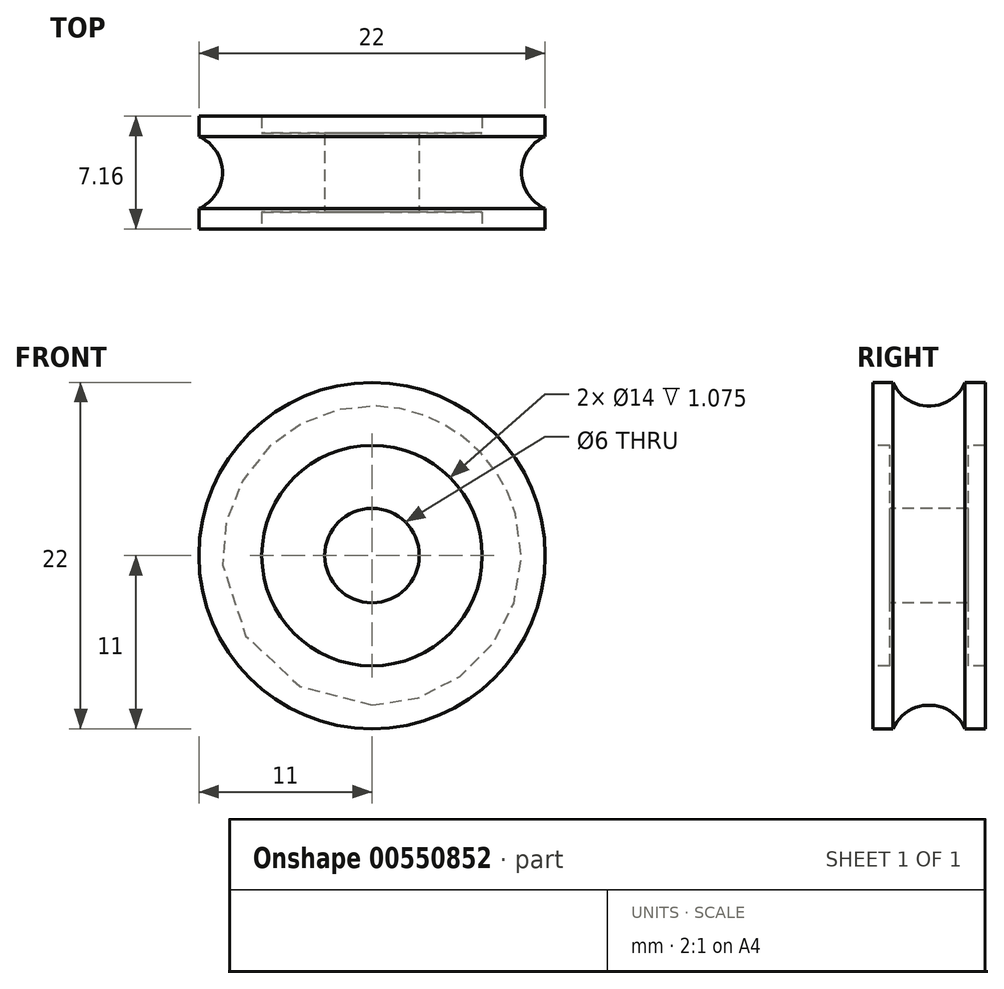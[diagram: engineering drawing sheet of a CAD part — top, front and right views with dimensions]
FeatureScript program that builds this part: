
annotation { "Feature Type Name" : "Feature", "Feature Type Description" : "" }
export const myFeature = defineFeature(function(context is Context, id is Id, definition is map)
    precondition{}
    {
        {
            var Q0;
            Q0=qCreatedBy(makeId("Right.planeOp"),FACE);
            var sketch = newSketch(context, id + "F0", { "sketchPlane" : qUnion([Q0])});
            skLineSegment(sketch, "E0", {"start": v(0, 0) * mm, "end": v(9.5, 0) * mm, "construction": true});
            skLineSegment(sketch, "E1", {"start": v(0, 0) * mm, "end": v(0, 3) * mm, "construction": true});
            skLineSegment(sketch, "E2", {"start": v(-2.5, 3) * mm, "end": v(2.5, 3) * mm});
            skLineSegment(sketch, "E3", {"start": v(2.5, 3) * mm, "end": v(2.5, 7) * mm});
            skLineSegment(sketch, "E4", {"start": v(2.5, 7) * mm, "end": v(3.58, 7) * mm});
            skLineSegment(sketch, "E5", {"start": v(3.58, 7) * mm, "end": v(3.58, 11) * mm});
            skLineSegment(sketch, "E6", {"start": v(3.58, 11) * mm, "end": v(2.3, 11) * mm});
            skLineSegment(sketch, "E7.MirrorCS", {"start": v(-2.5, 3) * mm, "end": v(-2.5, 7) * mm});
            skLineSegment(sketch, "E8.MirrorCS", {"start": v(-2.5, 7) * mm, "end": v(-3.58, 7) * mm});
            skLineSegment(sketch, "E9.MirrorCS", {"start": v(-3.58, 7) * mm, "end": v(-3.58, 11) * mm});
            skLineSegment(sketch, "E10.MirrorCS", {"start": v(-3.58, 11) * mm, "end": v(-2.3, 11) * mm});
            skArc(sketch, "E11", {"start": v(-2.3, 11) * mm, "mid": v(0, 9.5) * mm, "end": v(2.3, 11) * mm});
            skPoint(sketch, "E12", {"position": v(0, 9.5) * mm});
            skSolve(sketch);
        }
        {
            var Q0;
            Q0 = qSketchRegion(id + "F0", true);
            var Q1;
            Q1=sQuery(id+"F0.wireOp",EDGE,"E0");
            revolve(context, id + "F1", {"entities" : qUnion([Q0]), "axis" : qUnion([Q1]), "revolveType" : RevolveType.FULL});
        }
    });
